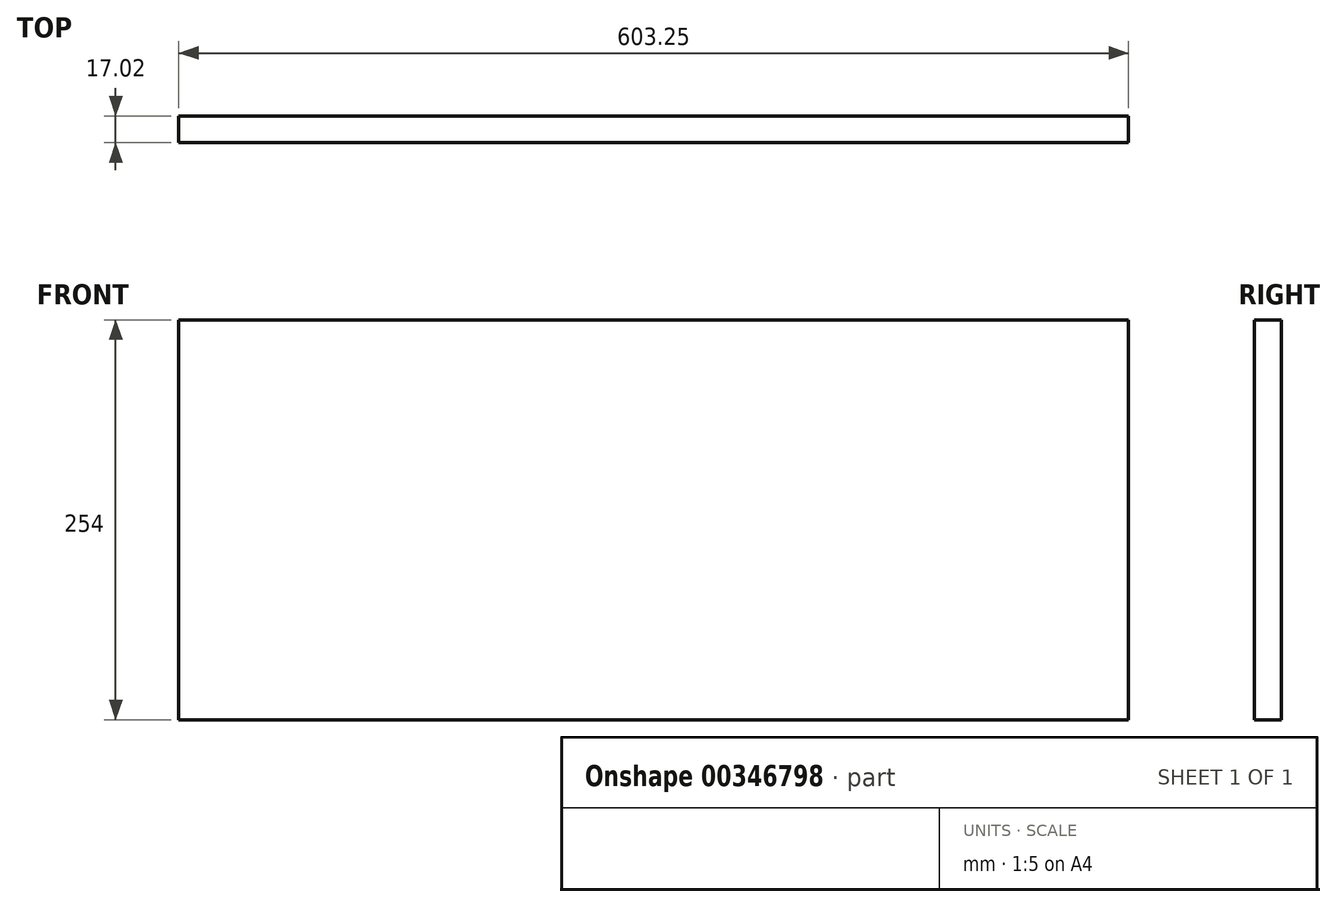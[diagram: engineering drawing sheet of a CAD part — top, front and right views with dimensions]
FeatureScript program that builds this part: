
annotation { "Feature Type Name" : "Feature", "Feature Type Description" : "" }
export const myFeature = defineFeature(function(context is Context, id is Id, definition is map)
    precondition{}
    {
        {
            var Q0;
            Q0=qCreatedBy(makeId("Front.planeOp"),FACE);
            var sketch = newSketch(context, id + "F0", { "sketchPlane" : qUnion([Q0])});
            skLineSegment(sketch, "E0.bottom", {"start": v(0, 0) * mm, "end": v(603.25, 0) * mm});
            skLineSegment(sketch, "E0.top", {"start": v(0, 254) * mm, "end": v(603.25, 254) * mm});
            skLineSegment(sketch, "E0.left", {"start": v(0, 0) * mm, "end": v(0, 254) * mm});
            skLineSegment(sketch, "E0.right", {"start": v(603.25, 0) * mm, "end": v(603.25, 254) * mm});
            skSolve(sketch);
        }
        {
            var Q0;
            Q0=makeQuery(id+"F0.imprint","IMPRINT",FACE,{"disambiguationData":[TD([[makeQuery(id+"F0.imprint","IMPRINT",EDGE,{"derivedFrom":sQuery(id+"F0.wireOp",EDGE,"E0.bottom")}),1.0]])]});
            extrude(context, id + "F1", {"entities" : qUnion([Q0]), "depth" : 17.02 * mm});
        }
    });
